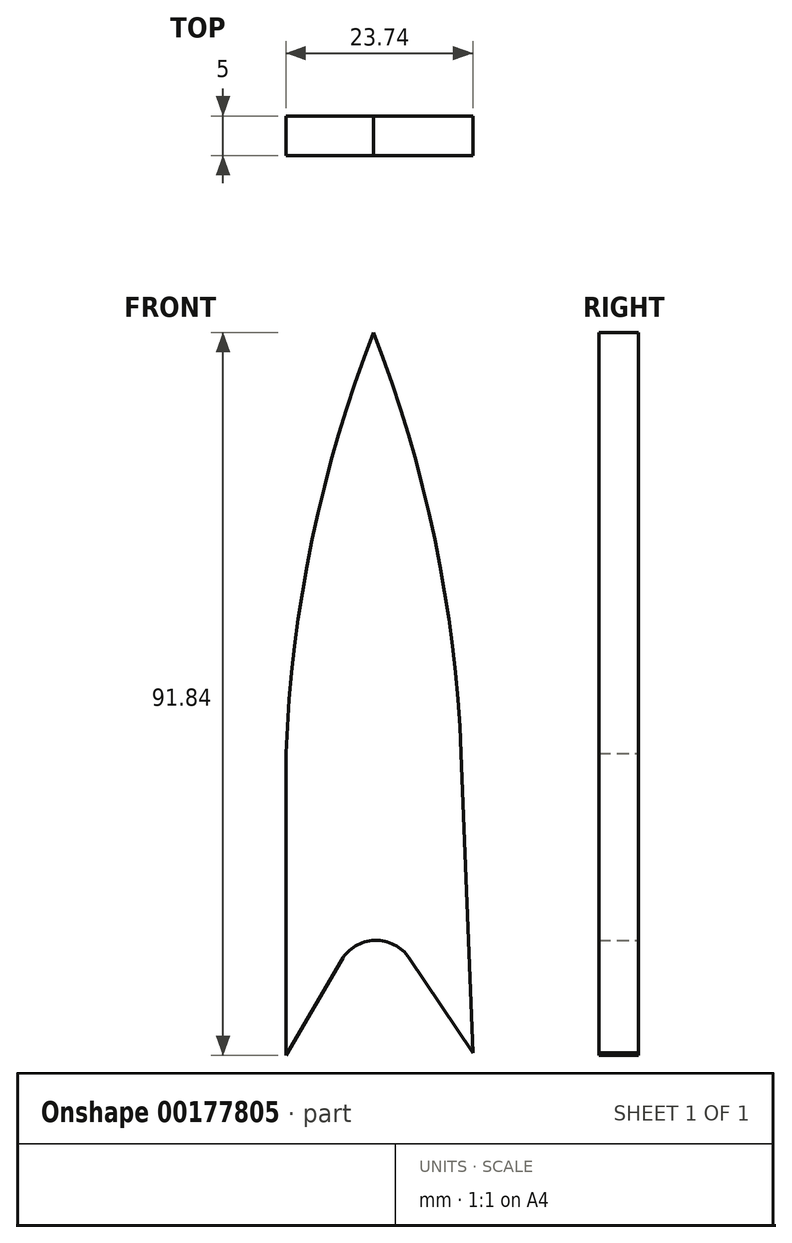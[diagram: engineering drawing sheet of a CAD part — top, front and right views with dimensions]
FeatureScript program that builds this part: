
annotation { "Feature Type Name" : "Feature", "Feature Type Description" : "" }
export const myFeature = defineFeature(function(context is Context, id is Id, definition is map)
    precondition{}
    {
        {
            var Q0;
            Q0=qCreatedBy(makeId("Front.planeOp"),FACE);
            var sketch = newSketch(context, id + "F0", { "sketchPlane" : qUnion([Q0])});
            skArc(sketch, "E0", {"start": v(0, 53.48) * mm, "mid": v(-7.78, 27.2) * mm, "end": v(-11.12, 0) * mm});
            skArc(sketch, "E1.MirrorCS", {"start": v(0, 53.48) * mm, "mid": v(7.78, 27.2) * mm, "end": v(11.12, 0) * mm});
            skLineSegment(sketch, "E2", {"start": v(-11.12, 0) * mm, "end": v(11.12, 0) * mm});
            skLineSegment(sketch, "E3", {"start": v(-11.12, 0) * mm, "end": v(-11.12, -38.36) * mm});
            skLineSegment(sketch, "E4", {"start": v(11.12, 0) * mm, "end": v(12.62, -38.03) * mm});
            skLineSegment(sketch, "E5", {"start": v(-11.12, -38.36) * mm, "end": v(-4.08, -26.26) * mm});
            skLineSegment(sketch, "E6", {"start": v(4.53, -25.99) * mm, "end": v(12.62, -38.03) * mm});
            skPoint(sketch, "E7.visualSharp", {"position": v(0, -19.25) * mm});
            skArc(sketch, "E7.filletArc", {"start": v(4.53, -25.99) * mm, "mid": v(0.15, -23.74) * mm, "end": v(-4.08, -26.26) * mm});
            skSolve(sketch);
        }
        {
            var Q0;
            Q0=makeQuery(id+"F0.imprint","IMPRINT",FACE,{"disambiguationData":[TD([[makeQuery(id+"F0.imprint","IMPRINT",EDGE,{"derivedFrom":sQuery(id+"F0.wireOp",EDGE,"E0")}),1.0]])]});
            extrude(context, id + "F1", {"entities" : qUnion([Q0]), "depth" : 5 * mm});
        }
        {
            var Q0;
            Q0=makeQuery(id+"F0.imprint","IMPRINT",FACE,{"disambiguationData":[TD([[makeQuery(id+"F0.imprint","IMPRINT",EDGE,{"derivedFrom":sQuery(id+"F0.wireOp",EDGE,"E2")}),-1.0]])]});
            extrude(context, id + "F2", {"entities" : qUnion([Q0]), "operationType" : NewBodyOperationType.ADD, "depth" : 5 * mm});
        }
    });
